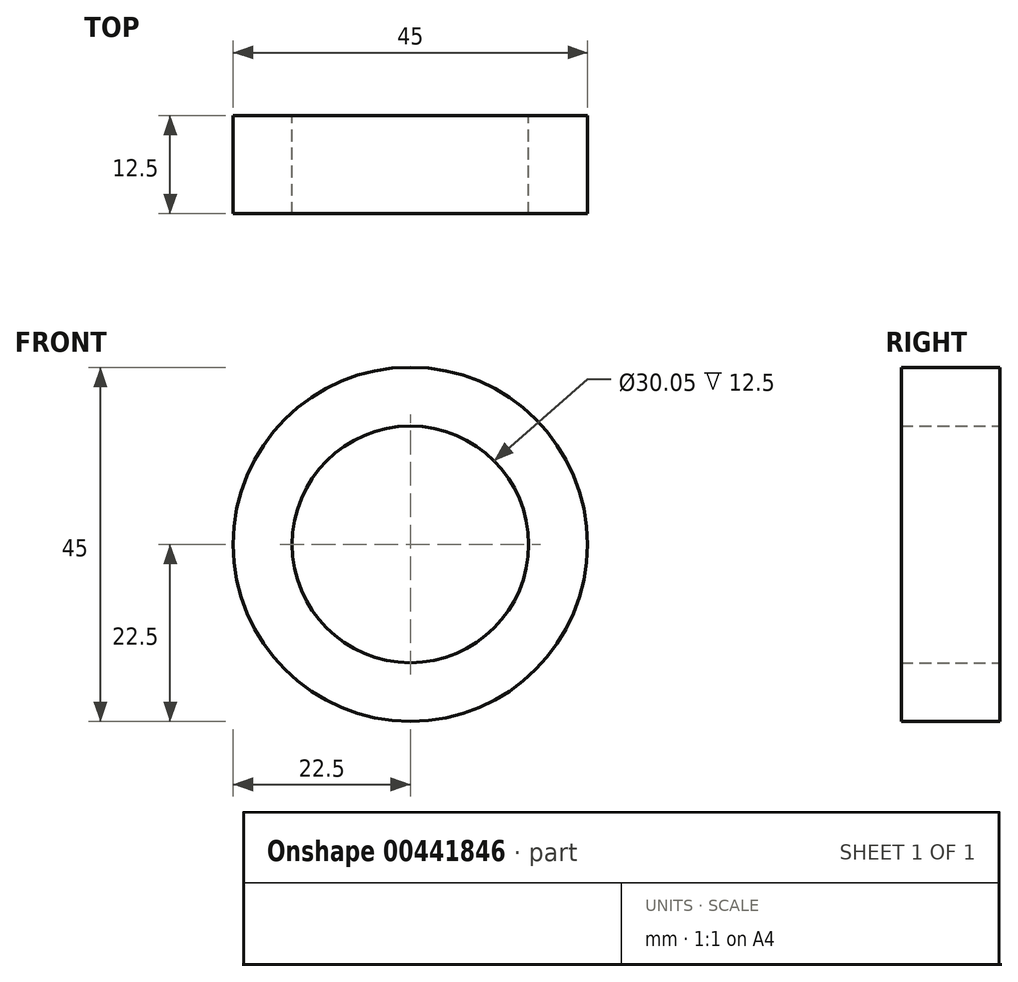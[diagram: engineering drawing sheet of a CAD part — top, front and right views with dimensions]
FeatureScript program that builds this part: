
annotation { "Feature Type Name" : "Feature", "Feature Type Description" : "" }
export const myFeature = defineFeature(function(context is Context, id is Id, definition is map)
    precondition{}
    {
        {
            var Q0;
            Q0=qCreatedBy(makeId("Front.planeOp"),FACE);
            var sketch = newSketch(context, id + "F0", { "sketchPlane" : qUnion([Q0])});
            skCircle(sketch, "E0", {"center": v(0, 0) * mm, "radius": 15.03 * mm});
            skCircle(sketch, "E1", {"center": v(0, 0) * mm, "radius": 22.5 * mm});
            skSolve(sketch);
        }
        {
            var Q0;
            Q0=makeQuery(id+"F0.imprint","IMPRINT",FACE,{"disambiguationData":[TD([[makeQuery(id+"F0.imprint","IMPRINT",EDGE,{"derivedFrom":sQuery(id+"F0.wireOp",EDGE,"E0")}),-1.0]])]});
            extrude(context, id + "F1", {"entities" : qUnion([Q0]), "depth" : 12.5 * mm});
        }
    });
